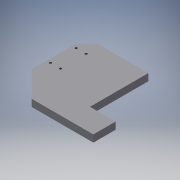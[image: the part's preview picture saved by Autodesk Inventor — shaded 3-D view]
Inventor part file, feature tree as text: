
AUTODESK INVENTOR PART (.ipt)
format: ipt  version: 2018 (Build 220112000, 112)  size: 142,336 bytes
history: native  units: mm
features: sketch x3, extrude x2, other x1, chamfer x1, hole x1
ambient origin geometry x8: Origin, YZ Plane, XZ Plane, XY Plane, X Axis, Y Axis, Z Axis, Center Point
bodies: Body1 (feature_tree)
feature tree (8):
  other  "Sólido1"
  extrude  "Extrusão1"  Depth=40.0mm
  chamfer  "Chanfro1"  Distance=98.71536mm
  hole  "Furo1"  [1 undecoded]
  extrude  "Extrusão2"  Depth=157.066236mm
  sketch  "Esboço1"  dims[d0=111.0mm d5=40.0mm]
  sketch  "Esboço2"  dims[d6=105.0mm]
  sketch  "Esboço3"  dims[d7=135.0deg d8=98.71536mm d9=12.7mm d10=0.0mm d11=157.066236mm d12=20.0mm d13=2.0mm d14=45.0deg d15=4.134mm d16=10.0mm d17=4.0mm d18=2.0mm d19=90.0deg d20=14.2mm d21=20.594885mm d22=35.0mm d23=35.0mm d24=2.0mm d25=10.0mm d26=0.0mm]
note: 1 required parameter value undecoded (feature->parameter linkage not recoverable at this tier; creation-order binding heuristic only, values carry confidence <= 0.55)
